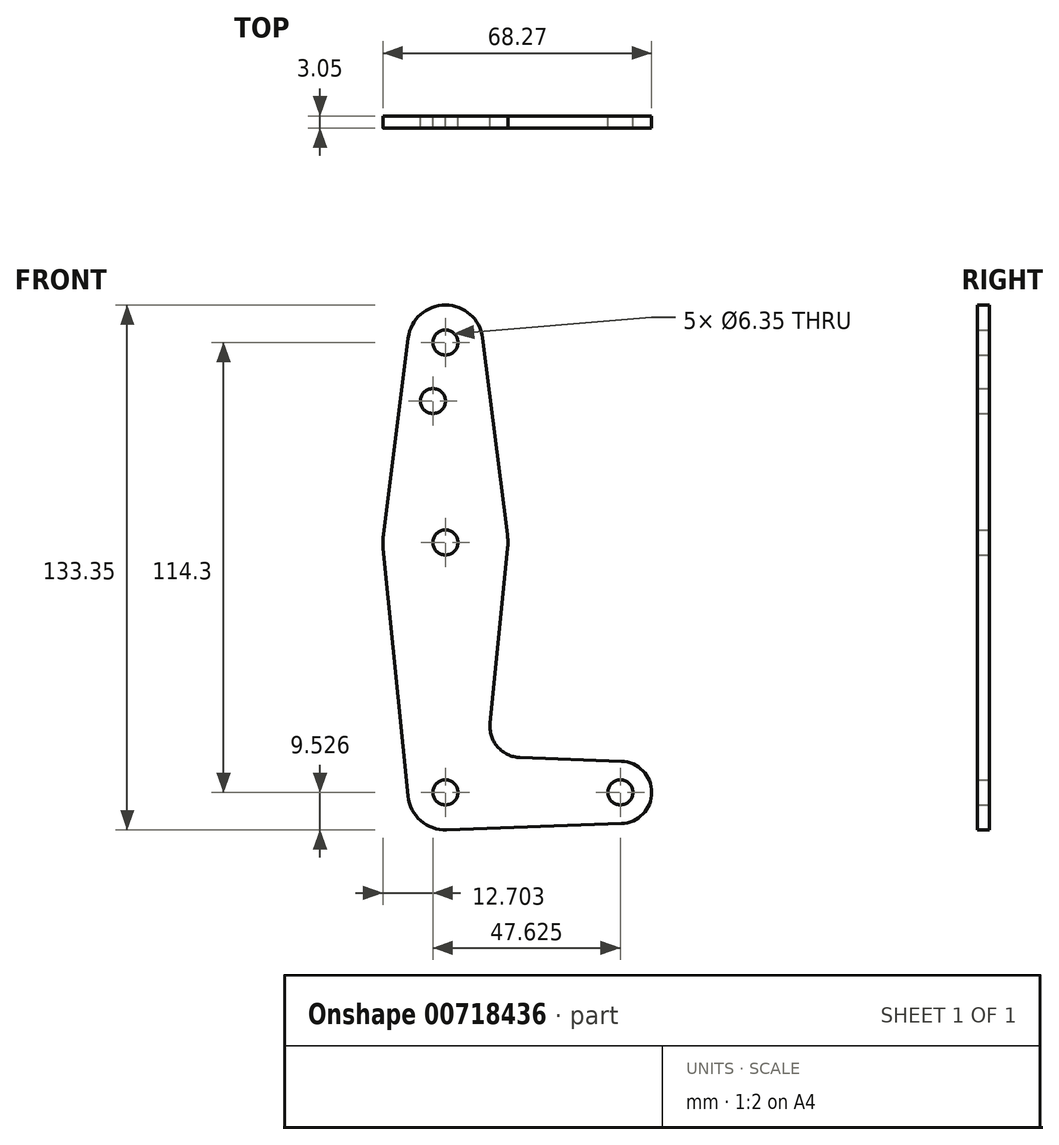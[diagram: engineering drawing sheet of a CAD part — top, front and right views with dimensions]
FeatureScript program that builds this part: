
annotation { "Feature Type Name" : "Feature", "Feature Type Description" : "" }
export const myFeature = defineFeature(function(context is Context, id is Id, definition is map)
    precondition{}
    {
        {
            var Q0;
            Q0=qCreatedBy(makeId("Front.planeOp"),FACE);
            var sketch = newSketch(context, id + "F0", { "sketchPlane" : qUnion([Q0])});
            skLineSegment(sketch, "E0", {"start": v(29.88, 76.72) * mm, "end": v(29.88, -37.58) * mm, "construction": true});
            skLineSegment(sketch, "E1", {"start": v(29.88, -37.58) * mm, "end": v(74.33, -37.58) * mm, "construction": true});
            skArc(sketch, "E2", {"start": v(39.33, 77.9) * mm, "mid": v(29.88, 86.24) * mm, "end": v(20.43, 77.9) * mm});
            skArc(sketch, "E3", {"start": v(14.13, 27.9) * mm, "mid": v(14, 26.12) * mm, "end": v(14.08, 24.33) * mm});
            skArc(sketch, "E4", {"start": v(20.4, -38.54) * mm, "mid": v(23.62, -44.76) * mm, "end": v(30.22, -47.1) * mm});
            skArc(sketch, "E5", {"start": v(74.61, -45.52) * mm, "mid": v(82.27, -37.58) * mm, "end": v(74.61, -29.65) * mm});
            skLineSegment(sketch, "E6", {"start": v(39.33, 77.9) * mm, "end": v(45.63, 27.9) * mm});
            skLineSegment(sketch, "E7", {"start": v(20.43, 77.9) * mm, "end": v(14.13, 27.9) * mm});
            skLineSegment(sketch, "E8", {"start": v(48.85, -28.73) * mm, "end": v(74.61, -29.65) * mm});
            skLineSegment(sketch, "E9", {"start": v(74.61, -45.52) * mm, "end": v(30.22, -47.1) * mm});
            skLineSegment(sketch, "E10", {"start": v(14.08, 24.33) * mm, "end": v(20.4, -38.54) * mm});
            skLineSegment(sketch, "E11", {"start": v(45.67, 24.33) * mm, "end": v(41.22, -20) * mm});
            skCircle(sketch, "E12", {"center": v(29.88, 76.72) * mm, "radius": 3.18 * mm});
            skCircle(sketch, "E13", {"center": v(29.88, 25.92) * mm, "radius": 3.18 * mm});
            skCircle(sketch, "E14", {"center": v(29.88, -37.58) * mm, "radius": 3.18 * mm});
            skCircle(sketch, "E15", {"center": v(74.33, -37.58) * mm, "radius": 3.18 * mm});
            skCircle(sketch, "E16", {"center": v(26.7, 61.85) * mm, "radius": 3.18 * mm});
            skArc(sketch, "E17.filletArc", {"start": v(41.22, -20) * mm, "mid": v(43.14, -26.01) * mm, "end": v(48.85, -28.73) * mm});
            skArc(sketch, "E18.trimOffspring", {"start": v(45.67, 24.33) * mm, "mid": v(45.75, 26.12) * mm, "end": v(45.63, 27.9) * mm});
            skSolve(sketch);
        }
        {
            var Q0;
            Q0 = qSketchRegion(id + "F0", true);
            extrude(context, id + "F1", {"entities" : qUnion([Q0]), "depth" : 3.05 * mm, "offsetDistance" : 25.4 * mm});
        }
    });
